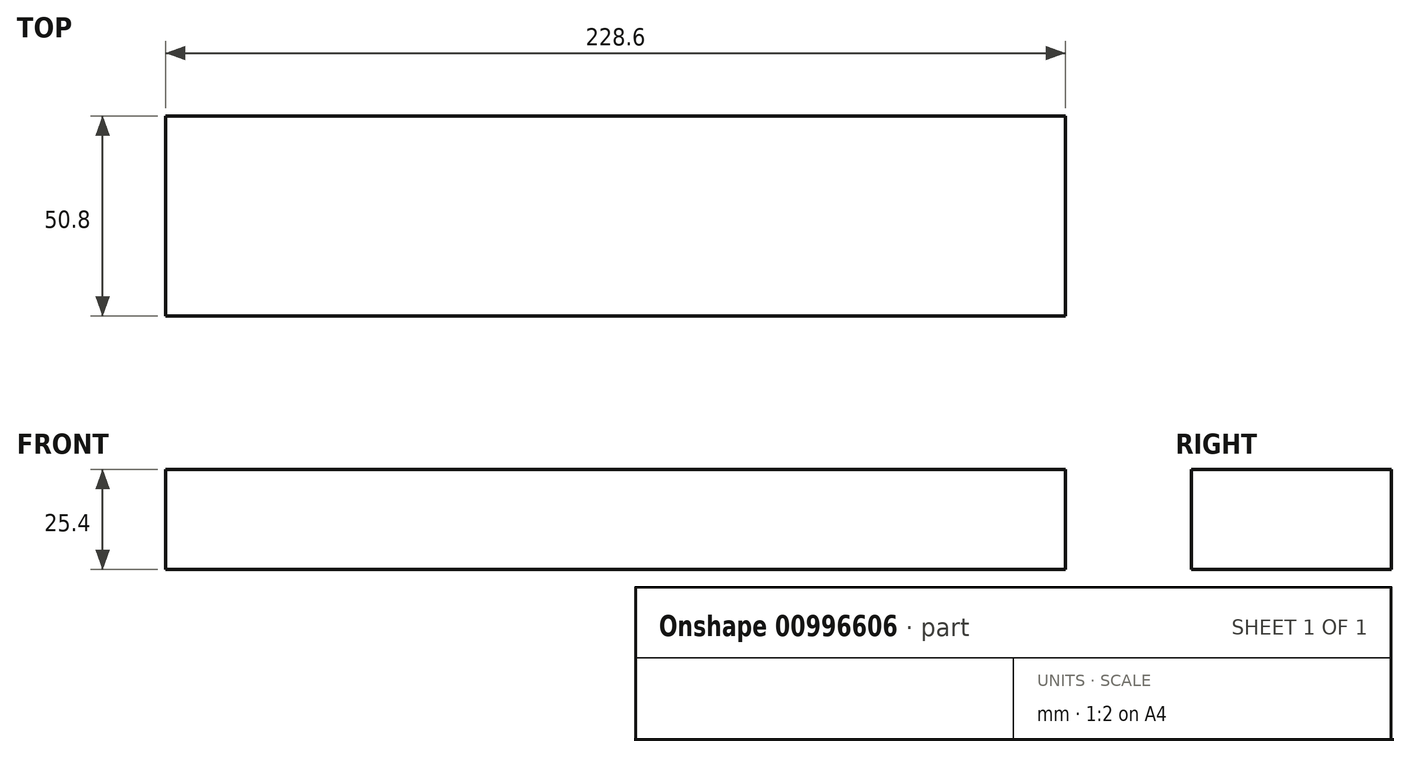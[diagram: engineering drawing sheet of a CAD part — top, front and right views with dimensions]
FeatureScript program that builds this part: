
annotation { "Feature Type Name" : "Feature", "Feature Type Description" : "" }
export const myFeature = defineFeature(function(context is Context, id is Id, definition is map)
    precondition{}
    {
        {
            var Q0;
            Q0=qCreatedBy(makeId("Top.planeOp"),FACE);
            var sketch = newSketch(context, id + "F0", { "sketchPlane" : qUnion([Q0])});
            skLineSegment(sketch, "E0.bottom", {"start": v(0, 0) * mm, "end": v(228.6, 0) * mm});
            skLineSegment(sketch, "E0.top", {"start": v(0, 50.8) * mm, "end": v(228.6, 50.8) * mm});
            skLineSegment(sketch, "E0.left", {"start": v(0, 0) * mm, "end": v(0, 50.8) * mm});
            skLineSegment(sketch, "E0.right", {"start": v(228.6, 0) * mm, "end": v(228.6, 50.8) * mm});
            skSolve(sketch);
        }
        {
            var Q0;
            Q0=makeQuery(id+"F0.imprint","IMPRINT",FACE,{"disambiguationData":[TD([[makeQuery(id+"F0.imprint","IMPRINT",EDGE,{"derivedFrom":sQuery(id+"F0.wireOp",EDGE,"E0.bottom")}),1.0]])]});
            extrude(context, id + "F1", {"entities" : qUnion([Q0]), "depth" : 25.4 * mm, "offsetDistance" : 25.4 * mm});
        }
    });
